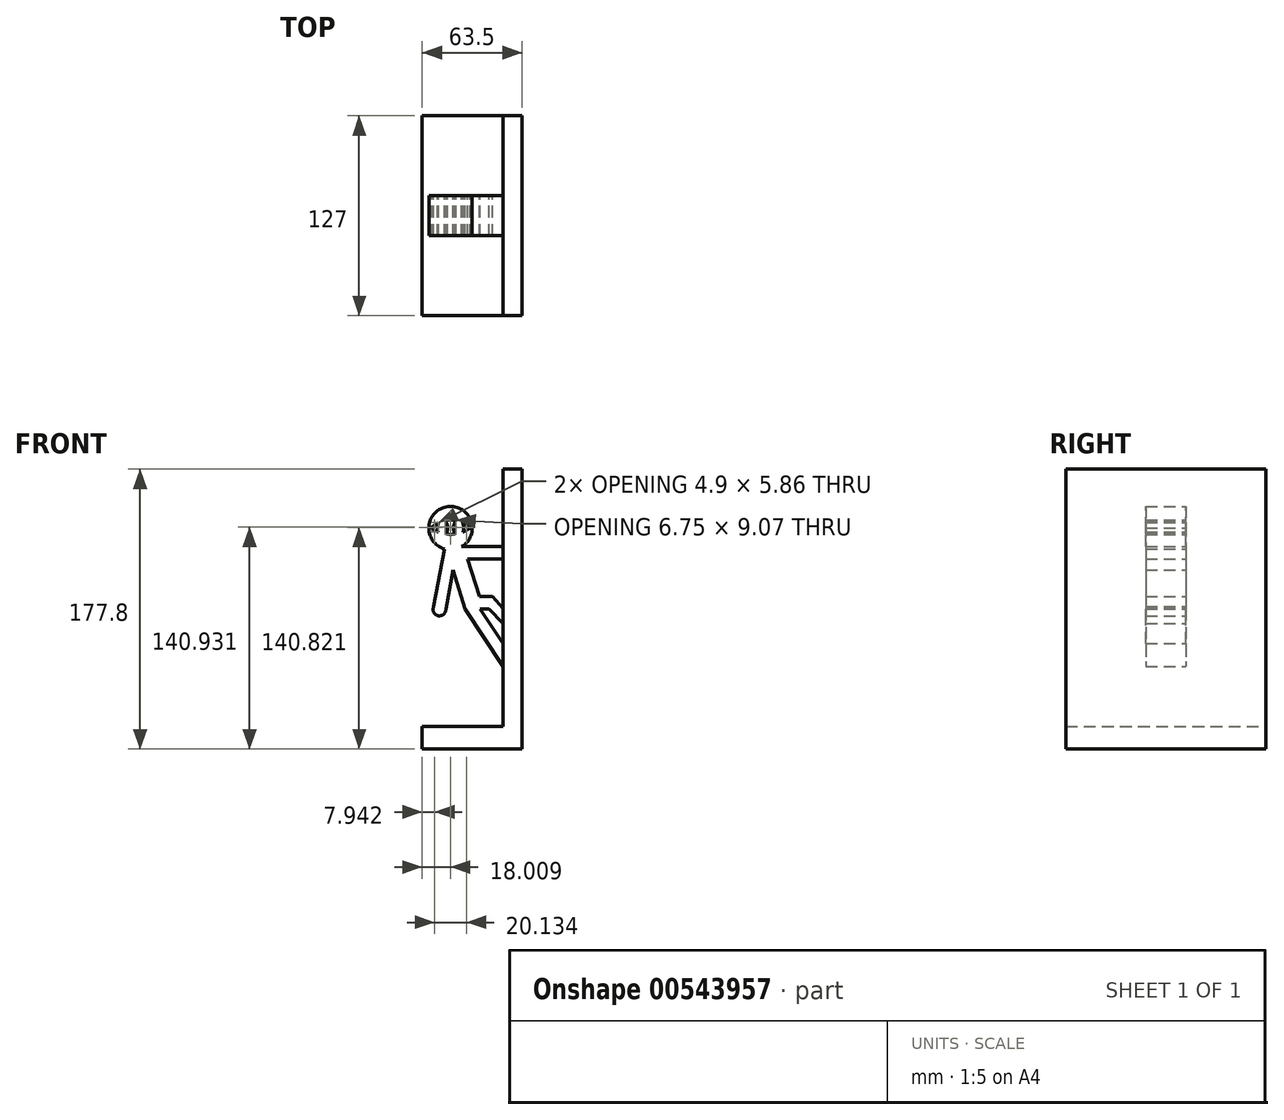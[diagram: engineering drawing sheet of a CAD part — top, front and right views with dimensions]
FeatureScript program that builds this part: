
annotation { "Feature Type Name" : "Feature", "Feature Type Description" : "" }
export const myFeature = defineFeature(function(context is Context, id is Id, definition is map)
    precondition{}
    {
        {
            var Q0;
            Q0=qCreatedBy(makeId("Front.planeOp"),FACE);
            var sketch = newSketch(context, id + "F0", { "sketchPlane" : qUnion([Q0])});
            skLineSegment(sketch, "E0.bottom", {"start": v(5.37, 97.97) * mm, "end": v(-6.86, 97.97) * mm});
            skLineSegment(sketch, "E0.top", {"start": v(5.37, -79.83) * mm, "end": v(-6.86, -79.83) * mm});
            skLineSegment(sketch, "E0.left", {"start": v(5.37, 97.97) * mm, "end": v(5.37, -79.83) * mm});
            skLineSegment(sketch, "E0.right", {"start": v(-6.86, 97.97) * mm, "end": v(-6.86, 48.68) * mm});
            skLineSegment(sketch, "E1.bottom", {"start": v(5.37, -79.83) * mm, "end": v(-58.13, -79.83) * mm});
            skLineSegment(sketch, "E1.top", {"start": v(-6.86, -65.52) * mm, "end": v(-58.13, -65.52) * mm});
            skLineSegment(sketch, "E1.left", {"start": v(5.37, -79.83) * mm, "end": v(5.37, -65.52) * mm});
            skLineSegment(sketch, "E1.right", {"start": v(-58.13, -79.83) * mm, "end": v(-58.13, -65.52) * mm});
            skLineSegment(sketch, "E2", {"start": v(-15.7, 9.27) * mm, "end": v(-6.86, 0) * mm});
            skArc(sketch, "E3", {"start": v(-33.01, 48.68) * mm, "mid": v(-41.87, 74.17) * mm, "end": v(-44.03, 47.27) * mm});
            skLineSegment(sketch, "E4", {"start": v(-33.01, 48.68) * mm, "end": v(-6.86, 48.68) * mm});
            skLineSegment(sketch, "E5", {"start": v(-6.86, 40.98) * mm, "end": v(-29.32, 40.98) * mm});
            skLineSegment(sketch, "E6", {"start": v(-29.32, 40.98) * mm, "end": v(-21.67, 17.14) * mm});
            skLineSegment(sketch, "E7", {"start": v(-21.67, 17.14) * mm, "end": v(-13.61, 17.14) * mm});
            skLineSegment(sketch, "E8", {"start": v(-13.61, 17.14) * mm, "end": v(-6.86, 9.41) * mm});
            skLineSegment(sketch, "E9", {"start": v(-44.03, 47.27) * mm, "end": v(-50.8, 10.61) * mm});
            skLineSegment(sketch, "E10", {"start": v(-43.15, 9.2) * mm, "end": v(-38.65, 33.76) * mm});
            skLineSegment(sketch, "E11", {"start": v(-38.65, 33.76) * mm, "end": v(-30.88, 9.2) * mm});
            skLineSegment(sketch, "E12", {"start": v(-30.88, 9.2) * mm, "end": v(-6.86, -27.48) * mm});
            skLineSegment(sketch, "E13", {"start": v(-6.86, -12.84) * mm, "end": v(-21.31, 9.2) * mm});
            skLineSegment(sketch, "E14", {"start": v(-21.31, 9.2) * mm, "end": v(-15.7, 9.27) * mm});
            skArc(sketch, "E15", {"start": v(-50.8, 10.61) * mm, "mid": v(-47.91, 4.84) * mm, "end": v(-43.15, 9.2) * mm});
            skLineSegment(sketch, "E16.trimOffspring", {"start": v(-6.86, 40.98) * mm, "end": v(-6.86, 9.41) * mm});
            skLineSegment(sketch, "E17.trimOffspring", {"start": v(-6.86, 0) * mm, "end": v(-6.86, -12.84) * mm});
            skLineSegment(sketch, "E18.trimOffspring", {"start": v(-6.86, -27.48) * mm, "end": v(-6.86, -65.52) * mm});
            skLineSegment(sketch, "E19", {"start": v(-6.86, 48.68) * mm, "end": v(-6.86, 40.98) * mm});
            skLineSegment(sketch, "E20", {"start": v(-6.86, 9.41) * mm, "end": v(-6.86, 0) * mm});
            skLineSegment(sketch, "E21", {"start": v(-6.86, -12.84) * mm, "end": v(-6.86, -27.48) * mm});
            skArc(sketch, "E22", {"start": v(-27.6, 60.5) * mm, "mid": v(-29.9, 62.41) * mm, "end": v(-32.5, 63.92) * mm});
            skArc(sketch, "E23", {"start": v(-52.64, 60.5) * mm, "mid": v(-50.43, 59.14) * mm, "end": v(-48.07, 58.06) * mm});
            skEllipticalArc(sketch, "E24", {});
            skEllipticalArc(sketch, "E25", {});
            skEllipticalArc(sketch, "E26.trimOffspring", {});
            skEllipticalArc(sketch, "E27.trimOffspring", {});
            skArc(sketch, "E28.trimOffspring", {"start": v(-42.8, 56.73) * mm, "mid": v(-40.12, 56.57) * mm, "end": v(-37.43, 56.73) * mm});
            skArc(sketch, "E29.trimOffspring", {"start": v(-47.74, 63.92) * mm, "mid": v(-50.33, 62.41) * mm, "end": v(-52.64, 60.5) * mm});
            skArc(sketch, "E30.trimOffspring", {"start": v(-36.75, 65.31) * mm, "mid": v(-40.12, 65.64) * mm, "end": v(-43.5, 65.31) * mm});
            skArc(sketch, "E31.trimOffspring", {"start": v(-32.17, 58.06) * mm, "mid": v(-29.81, 59.14) * mm, "end": v(-27.6, 60.5) * mm});
            const initialGuessF0  = {"E24": [-0.0452006351816671, 0.06049144268035889, 0, -1, 0.005715, 0.003175, 0.8526714179089928, 2.5748864382168555], "E25": [-0.03504063518166709, 0.06049144268035889, 0, 1, 0.005715, 0.003175, 0.5667062153729387, 2.2889212356808017], "E26.trimOffspring": [-0.0452006351816671, 0.06049144268035889, 0, -1, 0.005715, 0.003175, 4.068461221328021, 5.151853475570775], "E27.trimOffspring": [-0.03504063518166709, 0.06049144268035889, 0, 1, 0.005715, 0.003175, 4.2729244851986055, 5.356316739441355]};
            skSetInitialGuess(sketch, initialGuessF0);
            skSolve(sketch);
        }
        {
            var Q0;
            Q0=makeQuery(id+"F0.imprint","IMPRINT",FACE,{"disambiguationData":[TD([[makeQuery(id+"F0.imprint","IMPRINT",EDGE,{"derivedFrom":sQuery(id+"F0.wireOp",EDGE,"E0.bottom")}),1.0]])]});
            extrude(context, id + "F1", {"entities" : qUnion([Q0]), "depth" : 63.5 * mm, "offsetDistance" : 25.4 * mm, "hasSecondDirection" : true, "secondDirectionOppositeDirection" : true, "secondDirectionDepth" : 63.5 * mm});
        }
        {
            var Q0;
            Q0=makeQuery(id+"F0.imprint","IMPRINT",FACE,{"disambiguationData":[TD([[makeQuery(id+"F0.imprint","IMPRINT",EDGE,{"derivedFrom":sQuery(id+"F0.wireOp",EDGE,"E3")}),1.0]])]});
            var Q1;
            Q1=sQuery(id+"F0.wireOp",EDGE,"E3");
            var Q2;
            Q2=sQuery(id+"F0.wireOp",EDGE,"E29.trimOffspring");
            var Q3;
            Q3=sQuery(id+"F0.wireOp",EDGE,"E23");
            var Q4;
            Q4=sQuery(id+"F0.wireOp",EDGE,"E26.trimOffspring");
            var Q5;
            Q5=sQuery(id+"F0.wireOp",EDGE,"E9");
            var Q6;
            Q6=sQuery(id+"F0.wireOp",EDGE,"E10");
            var Q7;
            Q7=sQuery(id+"F0.wireOp",EDGE,"E15");
            var Q8;
            Q8=sQuery(id+"F0.wireOp",EDGE,"E11");
            var Q9;
            Q9=sQuery(id+"F0.wireOp",EDGE,"E12");
            var Q10;
            Q10=sQuery(id+"F0.wireOp",EDGE,"E13");
            var Q11;
            Q11=sQuery(id+"F0.wireOp",EDGE,"E14");
            var Q12;
            Q12=sQuery(id+"F0.wireOp",EDGE,"E2");
            var Q13;
            Q13=sQuery(id+"F0.wireOp",EDGE,"E8");
            var Q14;
            Q14=sQuery(id+"F0.wireOp",EDGE,"E6");
            var Q15;
            Q15=sQuery(id+"F0.wireOp",EDGE,"E5");
            var Q16;
            Q16=sQuery(id+"F0.wireOp",EDGE,"E4");
            var Q17;
            Q17=sQuery(id+"F0.wireOp",EDGE,"E24");
            var Q18;
            Q18=sQuery(id+"F0.wireOp",EDGE,"E30.trimOffspring");
            var Q19;
            Q19=sQuery(id+"F0.wireOp",EDGE,"E25");
            var Q20;
            Q20=sQuery(id+"F0.wireOp",EDGE,"E28.trimOffspring");
            var Q21;
            Q21=sQuery(id+"F0.wireOp",EDGE,"E27.trimOffspring");
            var Q22;
            Q22=sQuery(id+"F0.wireOp",EDGE,"E31.trimOffspring");
            var Q23;
            Q23=sQuery(id+"F0.wireOp",EDGE,"E22");
            extrude(context, id + "F2", {"entities" : qUnion([Q0]), "operationType" : NewBodyOperationType.ADD, "surfaceEntities" : qUnion([Q1, Q2, Q3, Q4, Q5, Q6, Q7, Q8, Q9, Q10, Q11, Q12, Q13, Q14, Q15, Q16, Q17, Q18, Q19, Q20, Q21, Q22, Q23]), "depth" : 12.7 * mm, "offsetDistance" : 25.4 * mm, "hasSecondDirection" : true, "secondDirectionOppositeDirection" : true, "secondDirectionDepth" : 12.7 * mm});
        }
    });
